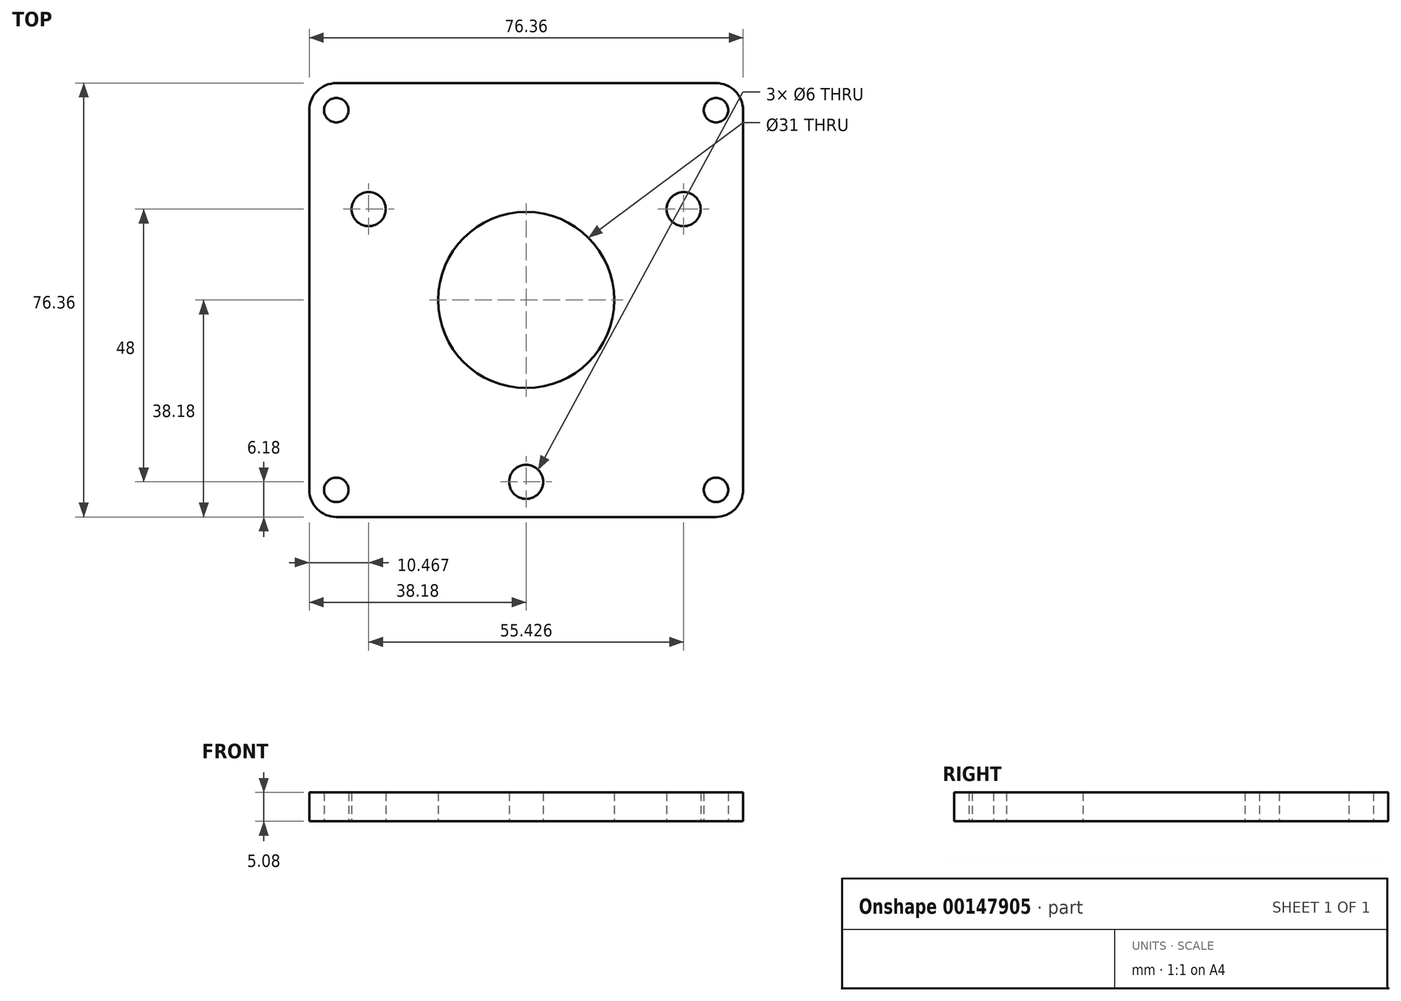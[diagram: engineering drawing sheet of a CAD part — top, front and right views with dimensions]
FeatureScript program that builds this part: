
annotation { "Feature Type Name" : "Feature", "Feature Type Description" : "" }
export const myFeature = defineFeature(function(context is Context, id is Id, definition is map)
    precondition{}
    {
        {
            var Q0;
            Q0=qCreatedBy(makeId("Top.planeOp"),FACE);
            var sketch = newSketch(context, id + "F0", { "sketchPlane" : qUnion([Q0])});
            skLineSegment(sketch, "E0", {"start": v(0, 0) * mm, "end": v(0, -32) * mm, "construction": true});
            skLineSegment(sketch, "E1", {"start": v(0, 0) * mm, "end": v(-27.71, 16) * mm, "construction": true});
            skLineSegment(sketch, "E2", {"start": v(0, 0) * mm, "end": v(27.71, 16) * mm, "construction": true});
            skLineSegment(sketch, "E3", {"start": v(0, -32) * mm, "end": v(-27.71, 16) * mm, "construction": true});
            skLineSegment(sketch, "E4", {"start": v(-27.71, 16) * mm, "end": v(27.71, 16) * mm, "construction": true});
            skLineSegment(sketch, "E5", {"start": v(27.71, 16) * mm, "end": v(0, -32) * mm, "construction": true});
            skCircle(sketch, "E6", {"center": v(0, 0) * mm, "radius": 15.5 * mm});
            skCircle(sketch, "E7", {"center": v(0, -32) * mm, "radius": 3 * mm});
            skCircle(sketch, "E8", {"center": v(27.71, 16) * mm, "radius": 3 * mm});
            skCircle(sketch, "E9", {"center": v(-27.71, 16) * mm, "radius": 3 * mm});
            skLineSegment(sketch, "E10.bottom", {"start": v(33.41, 33.41) * mm, "end": v(-33.41, 33.41) * mm, "construction": true});
            skLineSegment(sketch, "E10.top", {"start": v(33.41, -33.41) * mm, "end": v(-33.41, -33.41) * mm, "construction": true});
            skLineSegment(sketch, "E10.left", {"start": v(33.41, 33.41) * mm, "end": v(33.41, -33.41) * mm, "construction": true});
            skLineSegment(sketch, "E10.right", {"start": v(-33.41, 33.41) * mm, "end": v(-33.41, -33.41) * mm, "construction": true});
            skCircle(sketch, "E11", {"center": v(-33.41, 33.41) * mm, "radius": 2.15 * mm});
            skCircle(sketch, "E12", {"center": v(33.41, 33.41) * mm, "radius": 2.15 * mm});
            skCircle(sketch, "E13", {"center": v(33.41, -33.41) * mm, "radius": 2.15 * mm});
            skCircle(sketch, "E14", {"center": v(-33.41, -33.41) * mm, "radius": 2.15 * mm});
            skLineSegment(sketch, "E15.bottom", {"start": v(-38.18, 38.18) * mm, "end": v(38.18, 38.18) * mm});
            skLineSegment(sketch, "E15.top", {"start": v(-38.18, -38.18) * mm, "end": v(38.18, -38.18) * mm});
            skLineSegment(sketch, "E15.left", {"start": v(-38.18, 38.18) * mm, "end": v(-38.18, -38.18) * mm});
            skLineSegment(sketch, "E15.right", {"start": v(38.18, 38.18) * mm, "end": v(38.18, -38.18) * mm});
            skLineSegment(sketch, "E16", {"start": v(0, 33.41) * mm, "end": v(0, 38.18) * mm, "construction": true});
            skCircle(sketch, "E17", {"center": v(0, -32) * mm, "radius": 6.17 * mm, "construction": true});
            skCircle(sketch, "E18", {"center": v(0, 0) * mm, "radius": 38.18 * mm, "construction": true});
            skSolve(sketch);
        }
        {
            var Q0;
            Q0=qSketchRegion(id+"F0",true);
            extrude(context, id + "F1", {"entities" : qUnion([Q0]), "depth" : 5.08 * mm});
        }
        {
            var Q0;
            Q0=makeQuery(id+"F1.opExtrude","SWEPT_EDGE",EDGE,{"disambiguationData":[OSD([sQuery(id+"F0.wireOp",EDGE,"E15.bottom"),sQuery(id+"F0.wireOp",EDGE,"E15.left")])]});
            var Q1;
            Q1=makeQuery(id+"F1.opExtrude","SWEPT_EDGE",EDGE,{"disambiguationData":[OSD([sQuery(id+"F0.wireOp",EDGE,"E15.bottom"),sQuery(id+"F0.wireOp",EDGE,"E15.right")])]});
            var Q2;
            Q2=makeQuery(id+"F1.opExtrude","SWEPT_EDGE",EDGE,{"disambiguationData":[OSD([sQuery(id+"F0.wireOp",EDGE,"E15.top"),sQuery(id+"F0.wireOp",EDGE,"E15.right")])]});
            var Q3;
            Q3=makeQuery(id+"F1.opExtrude","SWEPT_EDGE",EDGE,{"disambiguationData":[OSD([sQuery(id+"F0.wireOp",EDGE,"E15.top"),sQuery(id+"F0.wireOp",EDGE,"E15.left")])]});
            fillet(context, id + "F2", {"entities" : qUnion([Q0, Q1, Q2, Q3]), "radius" : 4.76 * mm, "tangentPropagation" : true, "allowEdgeOverflow" : false});
        }
    });
